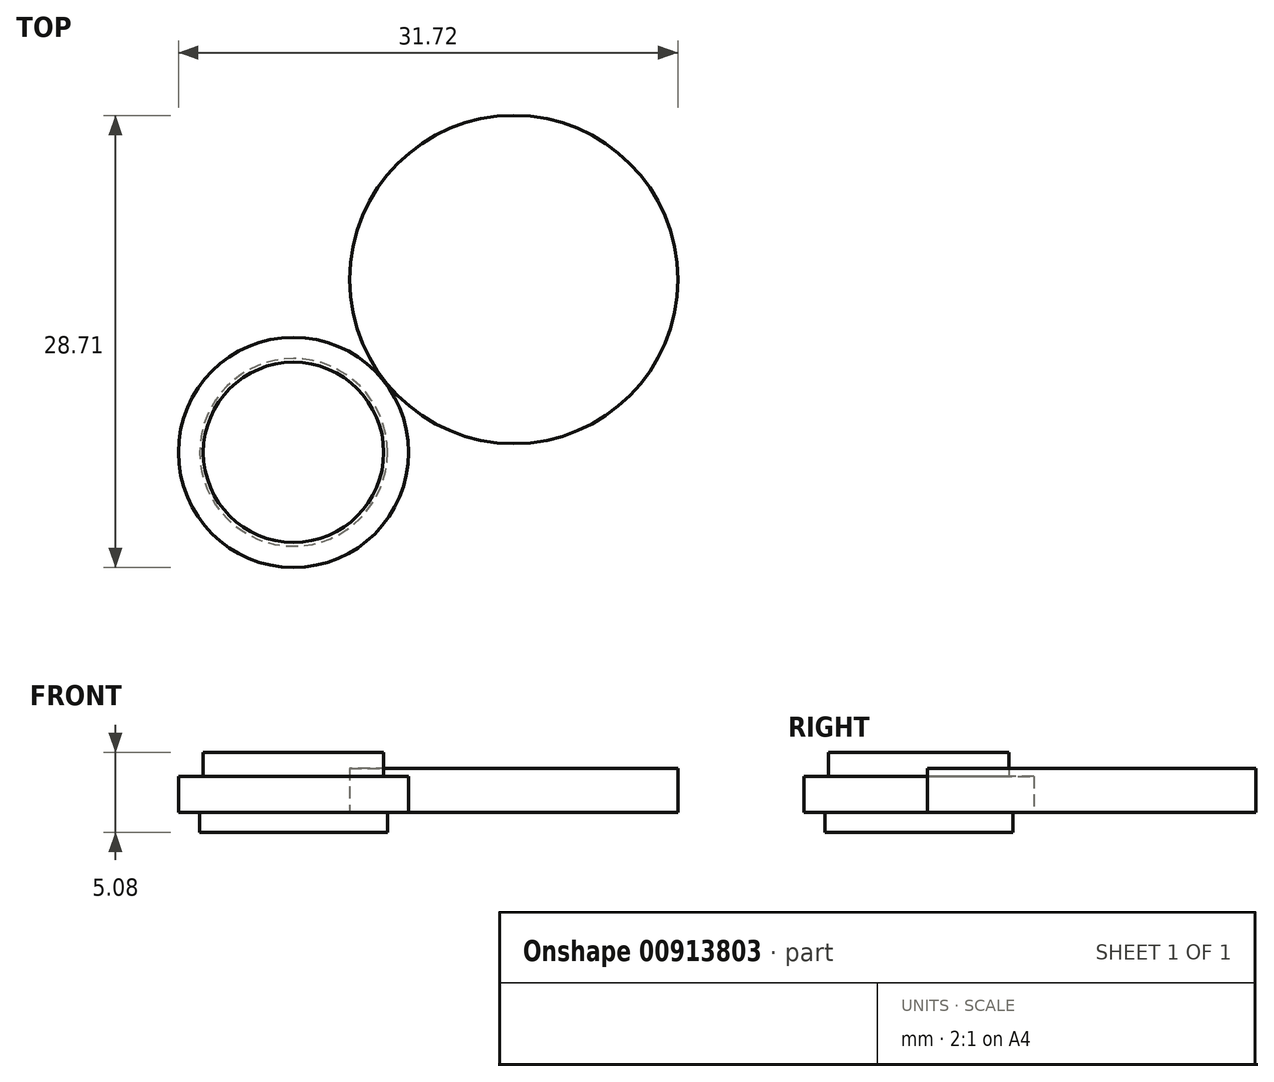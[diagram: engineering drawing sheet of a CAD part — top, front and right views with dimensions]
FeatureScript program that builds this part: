
annotation { "Feature Type Name" : "Feature", "Feature Type Description" : "" }
export const myFeature = defineFeature(function(context is Context, id is Id, definition is map)
    precondition{}
    {
        {
            var Q0;
            Q0=qCreatedBy(makeId("Top.planeOp"),FACE);
            var sketch = newSketch(context, id + "F0", { "sketchPlane" : qUnion([Q0])});
            skCircle(sketch, "E0", {"center": v(0, 0) * mm, "radius": 7.3 * mm});
            skSolve(sketch);
        }
        {
            var Q0;
            Q0 = qSketchRegion(id + "F0", true);
            extrude(context, id + "F1", {"entities" : qUnion([Q0]), "depth" : 2.3 * mm, "offsetDistance" : 25.4 * mm});
        }
        {
            var Q0;
            Q0=qCreatedBy(makeId("Top.planeOp"),FACE);
            var sketch = newSketch(context, id + "F2", { "sketchPlane" : qUnion([Q0])});
            skCircle(sketch, "E1", {"center": v(0, 0) * mm, "radius": 5.73 * mm});
            skSolve(sketch);
        }
        {
            var Q0;
            Q0 = qSketchRegion(id + "F2", true);
            extrude(context, id + "F3", {"entities" : qUnion([Q0]), "operationType" : NewBodyOperationType.ADD, "depth" : 3.8 * mm, "offsetDistance" : 25.4 * mm});
        }
        {
            var Q0;
            Q0=qCreatedBy(makeId("Top.planeOp"),FACE);
            var sketch = newSketch(context, id + "F4", { "sketchPlane" : qUnion([Q0])});
            skCircle(sketch, "E2", {"center": v(0, 0) * mm, "radius": 5.96 * mm});
            skSolve(sketch);
        }
        {
            var Q0;
            Q0 = qSketchRegion(id + "F4", true);
            extrude(context, id + "F5", {"entities" : qUnion([Q0]), "operationType" : NewBodyOperationType.ADD, "oppositeDirection" : true, "depth" : 1.27 * mm, "offsetDistance" : 25.4 * mm});
        }
        {
            var Q0;
            Q0=qCreatedBy(makeId("Top.planeOp"),FACE);
            var sketch = newSketch(context, id + "F6", { "sketchPlane" : qUnion([Q0])});
            skCircle(sketch, "E3", {"center": v(13.99, 10.98) * mm, "radius": 10.42 * mm});
            skSolve(sketch);
        }
        {
            var Q0;
            Q0 = qSketchRegion(id + "F6", true);
            extrude(context, id + "F7", {"entities" : qUnion([Q0]), "depth" : 2.8 * mm, "offsetDistance" : 25.4 * mm});
        }
    });
